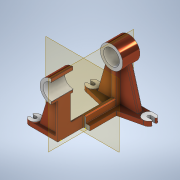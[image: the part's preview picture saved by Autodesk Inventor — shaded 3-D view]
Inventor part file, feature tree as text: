
AUTODESK INVENTOR PART (.ipt)
format: ipt  version: 2021 (Build 250183000, 183)  size: 594,944 bytes
history: native  units: in
note: dims shown in document units (in); Inventor stores cm internally (conversion verified against a paired STEP export)
features: sketch x33, extrude x26, fillet x5, chamfer x3, plane x2, mirror x1
ambient origin geometry x8: Origin, YZ Plane, XZ Plane, XY Plane, X Axis, Y Axis, Z Axis, Center Point
bodies: Solid1 (feature_tree)
feature tree (70):
  extrude  "Extrusion1"  Depth=0.5in
  extrude  "Extrusion2"  Depth=0.5in
  fillet  "Fillet1"  Radius=0.5in
  sketch  "Sketch3"  dims[d6=0.75in d7=0.5in]
  fillet  "Fillet2"  Radius=0.5in
  extrude  "Extrusion3"  Depth=0.5in
  sketch  "Sketch5"  dims[d12=3.0in d13=0.437in]
  sketch  "Sketch6"  dims[d14=0.188in d15=0.5in d16=0.0in]
  sketch  "Sketch7"  dims[d17=0.125in d18=0.125in]
  extrude  "Extrusion4"  Depth=0.5in
  fillet  "Fillet3"  Radius=5.0in
  sketch  "Sketch16"  dims[d19=0.03in d20=0.0in d21=0.5in d22=0.0in]
  sketch  "Sketch18"  dims[d23=0.05in d31=4.0in]
  extrude  "Extrusion6"  Depth=0.437in
  sketch  "Sketch20"  dims[d35=0.03in d36=0.0in d37=0.63in d38=0.0in]
  extrude  "Extrusion7"  Depth=0.5in TaperAngle=0.0deg
  extrude  "Extrusion8"  Depth=0.125in
  mirror  "Mirror1"
  extrude  "Extrusion9"  Depth=0.5in TaperAngle=0.0deg
  extrude  "Extrusion10"  Depth=4.0in
  extrude  "Extrusion11"  Depth=0.9375in
  extrude  "Extrusion12"  Depth=0.63in TaperAngle=0.0deg
  extrude  "Extrusion13"  Depth=1.5in TaperAngle=0.0deg
  extrude  "Extrusion14"  Depth=3.9375in TaperAngle=0.0deg
  extrude  "Extrusion15"  Depth=1.75in TaperAngle=0.0deg
  extrude  "Extrusion17"  Depth=6.0625in TaperAngle=0.0deg
  extrude  "Extrusion18"  Depth=0.25in TaperAngle=0.0deg
  extrude  "Extrusion19"  Depth=0.625in
  extrude  "Extrusion20"  Depth=0.5in TaperAngle=0.0deg
  extrude  "Extrusion21"  Depth=0.5in TaperAngle=0.0deg
  fillet  "Fillet4"  Radius=0.03in
  extrude  "Extrusion22"  Depth=0.125in TaperAngle=0.0deg
  sketch  "Sketch40"  dims[d55=1.0in d56=0.15in d57=0.25in]
  sketch  "Sketch41"  dims[d62=0.0625in]
  extrude  "Extrusion23"  Depth=1.75in TaperAngle=0.0deg
  extrude  "Extrusion24"  Depth=0.75in TaperAngle=0.0deg
  extrude  "Extrusion25"  Depth=3.0in TaperAngle=0.0deg
  extrude  "Extrusion26"  Depth=0.125in TaperAngle=90.0deg
  extrude  "Extrusion27"  Depth=0.125in TaperAngle=45.0deg
  extrude  "Extrusion28"  Depth=0.15in
  fillet  "Fillet5"  Radius=0.25in
  plane  "Work Plane1"
  plane  "Work Plane2"
  chamfer  "Chamfer1"  [1 undecoded]
  chamfer  "Chamfer2"  [1 undecoded]
  chamfer  "Chamfer3"  [1 undecoded]
  sketch  "Sketch1"  dims[d0=0.25in d1=0.5in]
  sketch  "Sketch2"  dims[d2=0.25in d3=0.5in d4=0.5in d5=0.5in]
  sketch  "Sketch4"  dims[d8=0.75in d9=0.5in d10=5.0in d11=0.0in]
  sketch  "Sketch19"  dims[d32=0.5in d33=0.9375in]
  sketch  "Sketch21"  dims[d39=1.5in d40=0.0in d41=1.5in d42=0.0in]
  sketch  "Sketch22"  dims[d43=1.5in d44=0.0in d45=3.9375in d46=0.0in]
  sketch  "Sketch23"  dims[d47=3.0in d48=0.0in d49=1.75in d50=0.0in]
  sketch  "Sketch24"  dims[d51=0.25in d52=0.0in d53=6.0625in d54=0.0in]
  sketch  "Sketch25"  dims[d58=0.25in d59=0.0in d60=0.25in d61=0.0in]
  sketch  "Sketch26"  dims[d66=2.5in d67=0.625in]
  sketch  "Sketch27"  dims[d68=0.188in d69=0.5in d70=0.0in]
  sketch  "Sketch28"  dims[d71=0.188in d72=0.5in d73=0.0in d74=0.03in d75=0.0in]
  sketch  "Sketch32"  dims[d76=0.125in d77=0.03in d78=0.0in]
  sketch  "Sketch33"  dims[d79=0.575in d80=0.0in d81=1.75in d82=0.0in]
  sketch  "Sketch36"  dims[d83=1.75in d84=0.0in d85=0.75in d86=0.0in]
  sketch  "Sketch37"  dims[d87=4.0625in d88=0.0in d89=3.0in d90=0.0in]
  sketch  "Sketch38"  dims[d91=0.125in d92=90.0deg d93=0.125in d94=0.125in d95=45.0deg]
  sketch  "Sketch39"  dims[d96=0.125in d97=0.125in d98=45.0deg d99=0.125in d100=0.125in d101=45.0deg]
  sketch  "Sketch42"  dims[d63=0.75in]
  sketch  "Sketch43"  dims[d64=0.375in]
  sketch  "Sketch44"
  sketch  "Sketch45"
  sketch  "Sketch46"
  sketch  "Sketch47"
note: 3 required parameter values undecoded (feature->parameter linkage not recoverable at this tier; creation-order binding heuristic only, values carry confidence <= 0.55)
